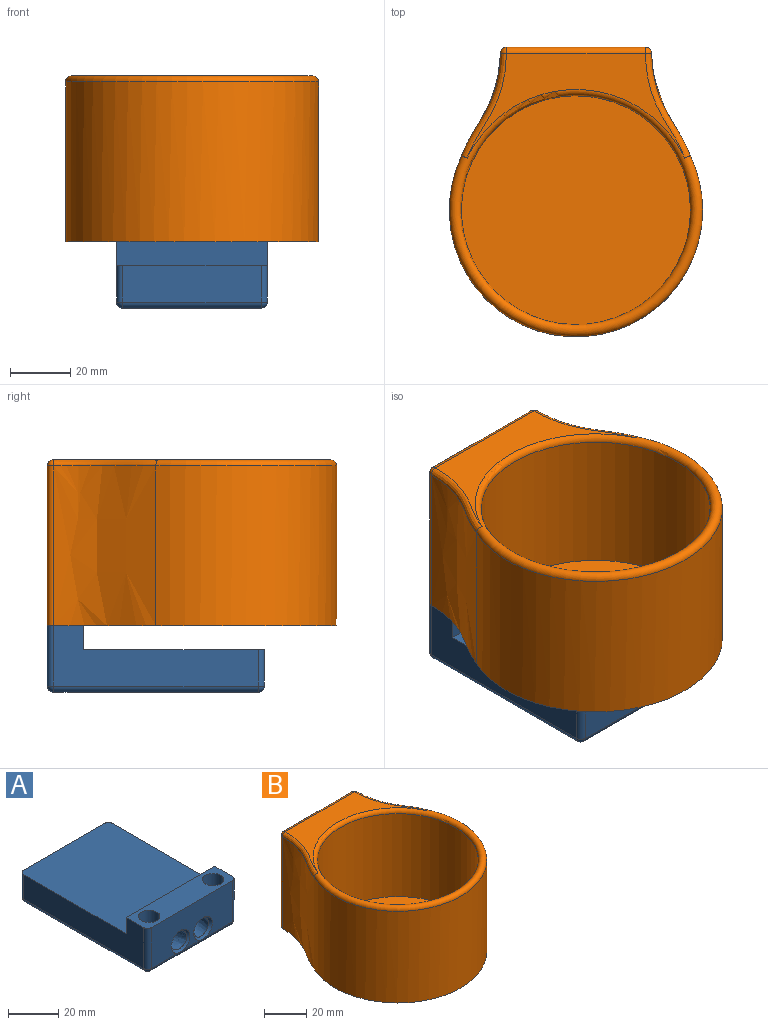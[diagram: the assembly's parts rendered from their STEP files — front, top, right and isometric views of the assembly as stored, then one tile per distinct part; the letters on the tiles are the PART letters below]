
ASSEMBLY  parts=2 mates=1
PART A: 32 faces, bbox 51.2x73.2x24.7 mm
  f0: plane 2.4x1.6mm, normal (0,0,-1), area 1.5mm2, adj f18,f28,f29
  f1: plane 68x46mm, normal (0,0,-1), area 2964.5mm2, adj f18,f19,f23,f24,f28,f29
  f2: plane 60x50mm, normal (0,0,1), area 2998.3mm2, adj f4,f5,f6,f8,f20,f22
  f3: plane 46.03x20.07mm, normal (0,-1,0), area 747.3mm2, adj f9,f16,f17,f25,f29,f31
  f4: plane 68x20mm, normal (1,0,0), area 896mm2, adj f2,f8,f9,f22,f28,f31
  f5: plane 46x12mm, normal (0,1,0), area 552mm2, adj f2,f20,f22,f23
  f6: plane 68x20mm, normal (-1,0,0), area 896mm2, adj f2,f8,f9,f20,f24,f25
  f7: plane 2.4x1.6mm, normal (0,0,-1), area 1.5mm2, adj f19,f24,f29
  f8: plane 50x8mm, normal (0,1,0), area 400mm2, adj f2,f4,f6,f9
  f9: plane 50x12mm, normal (0,0,1), area 484.8mm2, adj f3,f4,f6,f8,f10,f11,f25,f31
  f10: cylinder r=4.25mm len=21mm, axis (0,0,1), area 560.8mm2, adj f9,f18
  f11: cylinder r=4.25mm len=21mm, axis (0,0,1), area 560.8mm2, adj f9,f19
  f12: plane 9.68x9.68mm, normal (0,-1,0), area 56.7mm2, adj f13
  f13: bspline ~67x22.4mm, area 1790.2mm2, adj f12,f17
  f14: plane 9.68x9.68mm, normal (0,-1,0), area 56.7mm2, adj f15
  f15: bspline ~67x22.4mm, area 1779.2mm2, adj f14,f16
  f16: bspline ~10.54x10.5mm, area 42.2mm2, adj f3,f15,f29
  f17: bspline ~10.54x10.5mm, area 42.2mm2, adj f3,f13,f29
  f18: cone r=5.25mm half-angle=45deg, axis (0,0,-1), area 42.2mm2, adj f0,f1,f10,f28,f29
  f19: cone r=5.25mm half-angle=45deg, axis (0,0,-1), area 42.2mm2, adj f1,f7,f11,f24,f29
  f20: cylinder r=2mm len=12mm, axis (0,0,1), area 37.7mm2, adj f2,f5,f6,f21
  f21: sphere r=2mm, area 8.6mm2, adj f20,f23,f24
  f22: cylinder r=2mm len=12mm, axis (0,0,-1), area 37.7mm2, adj f2,f4,f5,f26
  f23: cylinder r=2mm len=46mm, axis (-1,0,0), area 144.5mm2, adj f1,f5,f21,f26
  f24: cylinder r=2mm len=68mm, axis (0,-1,0), area 213.1mm2, adj f1,f6,f7,f19,f21,f27
  f25: cylinder r=2mm len=20mm, axis (0,0,-1), area 62.8mm2, adj f3,f6,f9,f27
  f26: sphere r=2mm, area 4mm2, adj f22,f23,f28
  f27: sphere r=2mm, area 4mm2, adj f24,f25,f29
  f28: cylinder r=2mm len=68mm, axis (0,1,0), area 213.1mm2, adj f0,f1,f4,f18,f26,f30
  f29: cylinder r=2mm len=46mm, axis (1,0,0), area 133.7mm2, adj f0,f1,f3,f7,f16,f17,f18,f19
  f30: sphere r=2mm, area 6.3mm2, adj f28,f29,f31
  f31: cylinder r=2mm len=20mm, axis (0,0,1), area 62.8mm2, adj f3,f4,f9,f30
PART B: 20 faces, bbox 90.9x99.5x55 mm
  f0: plane 53x46.06mm, normal (0,1,0), area 2441mm2, adj f4,f12,f13,f14
  f1: extruded ~53x34.06mm, area 1958mm2, adj f2,f4,f13,f18
  f2: cylinder r=42mm len=84mm, axis (0,0,-1), area 8965mm2, adj f1,f3,f4,f19
  f3: extruded ~53x34.06mm, area 1958mm2, adj f2,f4,f12,f17
  f4: plane 96x84mm, normal (0,0,-1), area 6265.5mm2, adj f0,f1,f2,f3,f8,f10,f12,f13
  f5: cylinder r=38mm len=76mm, axis (0,0,-1), area 11460.5mm2, adj f7,f19
  f6: plane 72.21x34.79mm, normal (0,0,1), area 764.1mm2, adj f14,f17,f18,f19
  f7: plane 76x76mm, normal (0,0,1), area 4536.5mm2, adj f5
  f8: cylinder r=4.05mm len=40mm, axis (0,0,-1), area 1017.9mm2, adj f4,f9
  f9: plane 8.1x8.1mm, normal (0,0,-1), area 51.5mm2, adj f8
  f10: cylinder r=4.05mm len=40mm, axis (0,0,-1), area 1017.9mm2, adj f4,f11
  f11: plane 8.1x8.1mm, normal (0,0,-1), area 51.5mm2, adj f10
  f12: cylinder r=2mm len=53mm, axis (0,0,-1), area 163.5mm2, adj f0,f3,f4,f15
  f13: cylinder r=2mm len=53mm, axis (0,0,-1), area 163.5mm2, adj f0,f1,f4,f16
  f14: cylinder r=2mm len=46.06mm, axis (1,0,0), area 144.7mm2, adj f0,f6,f15,f16
  f15: sphere r=2mm, area 3.9mm2, adj f12,f14,f17
  f16: sphere r=2mm, area 8.5mm2, adj f13,f14,f18
  f17: bspline ~36.79x15.15mm, area 116.9mm2, adj f3,f6,f15,f19
  f18: bspline ~36.91x15.19mm, area 116.9mm2, adj f1,f6,f16,f19
  f19: torus R=40mm, axis (0,0,1), area 1287mm2, adj f2,f5,f6,f17,f18
PLACE A rot(axis=(0,0,1),180deg) t=(0,18,-27)mm
PLACE B t=(0,18,-5)mm
MATE fastened A.f10 <-> B.f8  axis (0,0,1) through (-18,48,-5)mm
